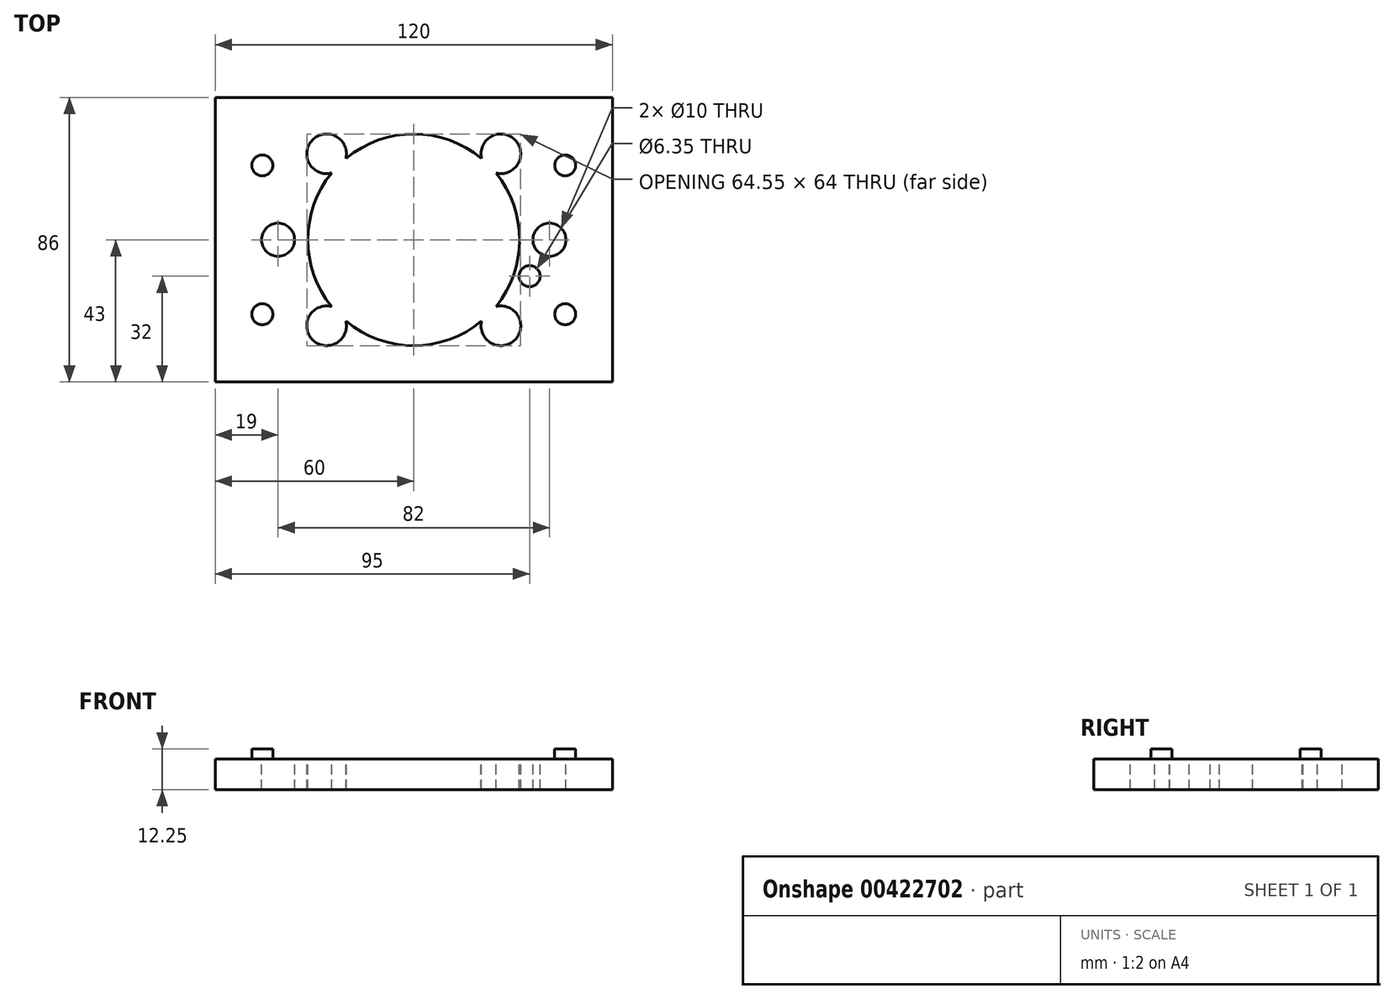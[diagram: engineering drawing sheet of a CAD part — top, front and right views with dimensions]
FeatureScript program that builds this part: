
annotation { "Feature Type Name" : "Feature", "Feature Type Description" : "" }
export const myFeature = defineFeature(function(context is Context, id is Id, definition is map)
    precondition{}
    {
        {
            var Q0;
            Q0=qCreatedBy(makeId("Top.planeOp"),FACE);
            var sketch = newSketch(context, id + "F0", { "sketchPlane" : qUnion([Q0])});
            skLineSegment(sketch, "E0", {"start": v(0, 60) * mm, "end": v(0, -60) * mm});
            skLineSegment(sketch, "E1", {"start": v(-70, 0) * mm, "end": v(70, 0) * mm});
            skLineSegment(sketch, "E2", {"start": v(-60, 43) * mm, "end": v(60, 43) * mm});
            skLineSegment(sketch, "E3", {"start": v(-60, -43) * mm, "end": v(60, -43) * mm});
            skCircle(sketch, "E4", {"center": v(-45.77, 22.5) * mm, "radius": 3.17 * mm});
            skCircle(sketch, "E5", {"center": v(-45.77, -22.5) * mm, "radius": 3.17 * mm});
            skCircle(sketch, "E6", {"center": v(45.77, -22.5) * mm, "radius": 3.17 * mm});
            skCircle(sketch, "E7", {"center": v(45.77, 22.5) * mm, "radius": 3.17 * mm});
            skCircle(sketch, "E8", {"center": v(-41, 0) * mm, "radius": 2.58 * mm});
            skCircle(sketch, "E9", {"center": v(41, 0) * mm, "radius": 2.58 * mm});
            skCircle(sketch, "E10", {"center": v(-41, 0) * mm, "radius": 5 * mm});
            skCircle(sketch, "E11", {"center": v(41, 0) * mm, "radius": 5 * mm});
            skLineSegment(sketch, "E12", {"start": v(60, 43) * mm, "end": v(60, -43) * mm});
            skLineSegment(sketch, "E13", {"start": v(-60, 43) * mm, "end": v(-60, -43) * mm});
            skArc(sketch, "E14", {"start": v(-24.83, 20.2) * mm, "mid": v(-32, 0) * mm, "end": v(-24.83, -20.2) * mm});
            skArc(sketch, "E15", {"start": v(-20.5, 24.57) * mm, "mid": v(-30.6, 30.22) * mm, "end": v(-24.83, 20.2) * mm});
            skArc(sketch, "E16", {"start": v(24.83, 20.2) * mm, "mid": v(30.6, 30.22) * mm, "end": v(20.5, 24.57) * mm});
            skArc(sketch, "E17", {"start": v(20.5, -24.57) * mm, "mid": v(30.6, -30.22) * mm, "end": v(24.83, -20.2) * mm});
            skArc(sketch, "E18", {"start": v(-24.83, -20.2) * mm, "mid": v(-30.6, -30.22) * mm, "end": v(-20.5, -24.57) * mm});
            skArc(sketch, "E19", {"start": v(20.5, 24.57) * mm, "mid": v(0, 32) * mm, "end": v(-20.5, 24.57) * mm});
            skArc(sketch, "E20", {"start": v(-20.5, -24.57) * mm, "mid": v(0, -32) * mm, "end": v(20.5, -24.57) * mm});
            skArc(sketch, "E21", {"start": v(24.83, -20.2) * mm, "mid": v(32, 0) * mm, "end": v(24.83, 20.2) * mm});
            skCircle(sketch, "E22", {"center": v(35, -11) * mm, "radius": 3.17 * mm});
            skSolve(sketch);
        }
        {
            var Q0;
            Q0=makeQuery(id+"F0.imprint","IMPRINT",FACE,{"disambiguationData":[TD([[makeQuery(id+"F0.imprint","IMPRINT",EDGE,{"derivedFrom":sQuery(id+"F0.wireOp",EDGE,"E7")}),1.0]])]});
            var Q1;
            Q1=makeQuery(id+"F0.imprint","IMPRINT",FACE,{"disambiguationData":[TD([[makeQuery(id+"F0.imprint","IMPRINT",EDGE,{"derivedFrom":sQuery(id+"F0.wireOp",EDGE,"E4")}),1.0]])]});
            var Q2;
            Q2=makeQuery(id+"F0.imprint","IMPRINT",FACE,{"disambiguationData":[TD([[makeQuery(id+"F0.imprint","IMPRINT",EDGE,{"derivedFrom":sQuery(id+"F0.wireOp",EDGE,"E5")}),1.0]])]});
            var Q3;
            Q3=makeQuery(id+"F0.imprint","IMPRINT",FACE,{"disambiguationData":[TD([[makeQuery(id+"F0.imprint","IMPRINT",EDGE,{"derivedFrom":sQuery(id+"F0.wireOp",EDGE,"E6")}),1.0]])]});
            var Q4;
            {var subQ0=sQuery(id+"F0.wireOp",EDGE,"E10");var subQ1=sQuery(id+"F0.wireOp",EDGE,"E1");var subQ2=makeQuery(id+"F0.imprint","INTERSECT",VERTEX,{"disambiguationData":[OD(0.0)],"derivedFrom":[subQ1,subQ0]});Q4=makeQuery(id+"F0.imprint","IMPRINT",FACE,{"disambiguationData":[TD([[makeQuery(id+"F0.imprint","IMPRINT",EDGE,{"disambiguationData":[TD([[subQ2,-1.0]])],"derivedFrom":subQ1}),-1.0]])]});}
            var Q5;
            {var subQ0=sQuery(id+"F0.wireOp",EDGE,"E10");var subQ1=sQuery(id+"F0.wireOp",EDGE,"E1");var subQ2=makeQuery(id+"F0.imprint","INTERSECT",VERTEX,{"disambiguationData":[OD(0.0)],"derivedFrom":[subQ1,subQ0]});Q5=makeQuery(id+"F0.imprint","IMPRINT",FACE,{"disambiguationData":[TD([[makeQuery(id+"F0.imprint","IMPRINT",EDGE,{"disambiguationData":[TD([[subQ2,-1.0]])],"derivedFrom":subQ1}),1.0]])]});}
            var Q6;
            {var subQ0=sQuery(id+"F0.wireOp",EDGE,"E11");var subQ1=sQuery(id+"F0.wireOp",EDGE,"E1");var subQ2=makeQuery(id+"F0.imprint","INTERSECT",VERTEX,{"disambiguationData":[OD(0.0)],"derivedFrom":[subQ1,subQ0]});Q6=makeQuery(id+"F0.imprint","IMPRINT",FACE,{"disambiguationData":[TD([[makeQuery(id+"F0.imprint","IMPRINT",EDGE,{"disambiguationData":[TD([[subQ2,-1.0]])],"derivedFrom":subQ1}),1.0]])]});}
            var Q7;
            {var subQ0=sQuery(id+"F0.wireOp",EDGE,"E11");var subQ1=sQuery(id+"F0.wireOp",EDGE,"E1");var subQ2=makeQuery(id+"F0.imprint","INTERSECT",VERTEX,{"disambiguationData":[OD(0.0)],"derivedFrom":[subQ1,subQ0]});Q7=makeQuery(id+"F0.imprint","IMPRINT",FACE,{"disambiguationData":[TD([[makeQuery(id+"F0.imprint","IMPRINT",EDGE,{"disambiguationData":[TD([[subQ2,-1.0]])],"derivedFrom":subQ1}),-1.0]])]});}
            extrude(context, id + "F1", {"entities" : qUnion([Q0, Q1, Q2, Q3, Q4, Q5, Q6, Q7]), "oppositeDirection" : true, "depth" : 12.25 * mm});
        }
        {
            var Q0;
            {var subQ0=sQuery(id+"F0.wireOp",EDGE,"E10");var subQ1=sQuery(id+"F0.wireOp",EDGE,"E1");var subQ2=makeQuery(id+"F0.imprint","INTERSECT",VERTEX,{"disambiguationData":[OD(0.0)],"derivedFrom":[subQ1,subQ0]});Q0=makeQuery(id+"F0.imprint","IMPRINT",FACE,{"disambiguationData":[TD([[makeQuery(id+"F0.imprint","IMPRINT",EDGE,{"disambiguationData":[TD([[subQ2,-1.0]])],"derivedFrom":subQ1}),-1.0]])]});}
            var Q1;
            {var subQ0=sQuery(id+"F0.wireOp",EDGE,"E10");var subQ1=sQuery(id+"F0.wireOp",EDGE,"E1");var subQ2=makeQuery(id+"F0.imprint","INTERSECT",VERTEX,{"disambiguationData":[OD(0.0)],"derivedFrom":[subQ1,subQ0]});Q1=makeQuery(id+"F0.imprint","IMPRINT",FACE,{"disambiguationData":[TD([[makeQuery(id+"F0.imprint","IMPRINT",EDGE,{"disambiguationData":[TD([[subQ2,-1.0]])],"derivedFrom":subQ1}),1.0]])]});}
            var Q2;
            {var subQ0=sQuery(id+"F0.wireOp",EDGE,"E11");var subQ1=sQuery(id+"F0.wireOp",EDGE,"E1");var subQ2=makeQuery(id+"F0.imprint","INTERSECT",VERTEX,{"disambiguationData":[OD(0.0)],"derivedFrom":[subQ1,subQ0]});Q2=makeQuery(id+"F0.imprint","IMPRINT",FACE,{"disambiguationData":[TD([[makeQuery(id+"F0.imprint","IMPRINT",EDGE,{"disambiguationData":[TD([[subQ2,-1.0]])],"derivedFrom":subQ1}),1.0]])]});}
            var Q3;
            {var subQ0=sQuery(id+"F0.wireOp",EDGE,"E11");var subQ1=sQuery(id+"F0.wireOp",EDGE,"E1");var subQ2=makeQuery(id+"F0.imprint","INTERSECT",VERTEX,{"disambiguationData":[OD(0.0)],"derivedFrom":[subQ1,subQ0]});Q3=makeQuery(id+"F0.imprint","IMPRINT",FACE,{"disambiguationData":[TD([[makeQuery(id+"F0.imprint","IMPRINT",EDGE,{"disambiguationData":[TD([[subQ2,-1.0]])],"derivedFrom":subQ1}),-1.0]])]});}
            extrude(context, id + "F2", {"entities" : qUnion([Q0, Q1, Q2, Q3]), "oppositeDirection" : true, "depth" : 3 * mm});
        }
        {
            var Q0;
            Q0=makeQuery(id+"F2.opExtrude","SWEPT_BODY",BODY,{"disambiguationData":[OSD([sQuery(id+"F0.wireOp",EDGE,"E8"),sQuery(id+"F0.wireOp",EDGE,"E10")])]});
            var Q1;
            Q1=makeQuery(id+"F2.opExtrude","SWEPT_BODY",BODY,{"disambiguationData":[OSD([sQuery(id+"F0.wireOp",EDGE,"E9"),sQuery(id+"F0.wireOp",EDGE,"E11")])]});
            var Q2;
            Q2=makeQuery(id+"F1.opExtrude","SWEPT_BODY",BODY,{"disambiguationData":[OSD([sQuery(id+"F0.wireOp",EDGE,"E2"),sQuery(id+"F0.wireOp",EDGE,"E3"),sQuery(id+"F0.wireOp",EDGE,"E4"),sQuery(id+"F0.wireOp",EDGE,"E5"),sQuery(id+"F0.wireOp",EDGE,"E6"),sQuery(id+"F0.wireOp",EDGE,"E7"),sQuery(id+"F0.wireOp",EDGE,"E8"),sQuery(id+"F0.wireOp",EDGE,"E9"),sQuery(id+"F0.wireOp",EDGE,"E12"),sQuery(id+"F0.wireOp",EDGE,"E13"),sQuery(id+"F0.wireOp",EDGE,"E14"),sQuery(id+"F0.wireOp",EDGE,"E15"),sQuery(id+"F0.wireOp",EDGE,"E16"),sQuery(id+"F0.wireOp",EDGE,"E17"),sQuery(id+"F0.wireOp",EDGE,"E18"),sQuery(id+"F0.wireOp",EDGE,"E19"),sQuery(id+"F0.wireOp",EDGE,"E20"),sQuery(id+"F0.wireOp",EDGE,"E21"),sQuery(id+"F0.wireOp",EDGE,"E22")])]});
            booleanBodies(context, id + "F3", {"operationType" : BooleanOperationType.SUBTRACTION, "tools" : qUnion([Q0, Q1]), "targets" : qUnion([Q2])});
        }
    });
